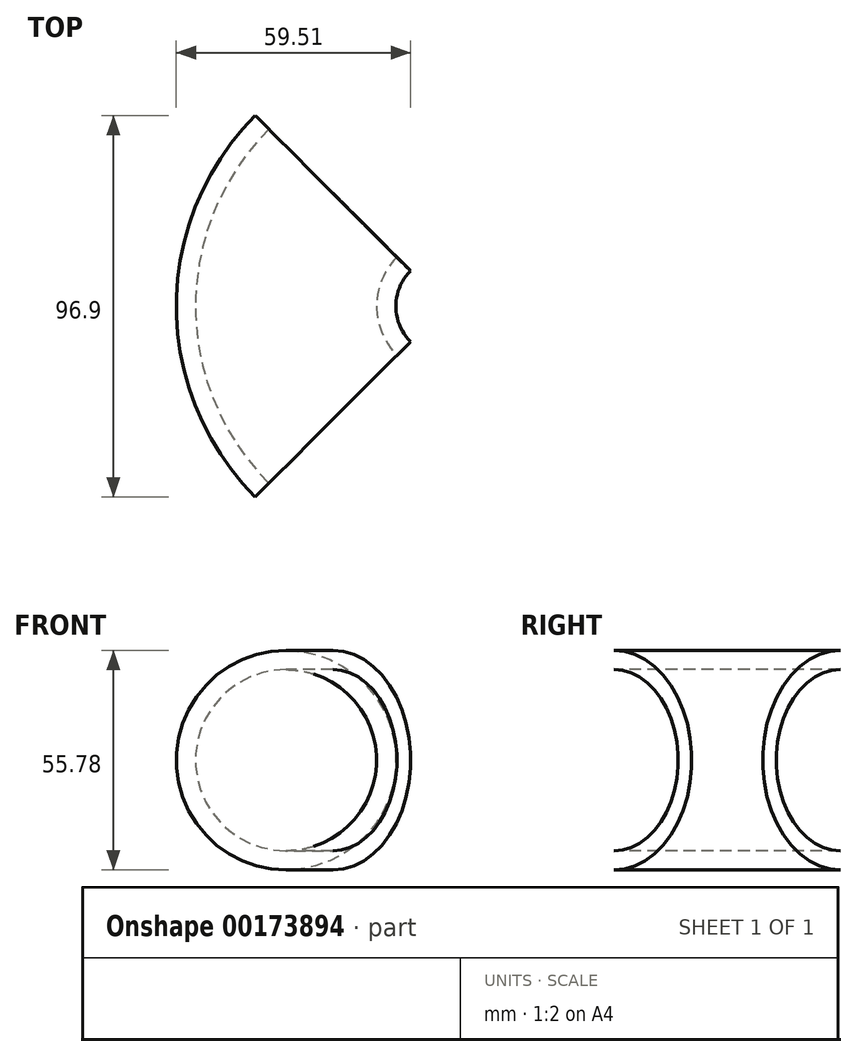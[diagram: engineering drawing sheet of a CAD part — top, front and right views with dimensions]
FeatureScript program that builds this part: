
annotation { "Feature Type Name" : "Feature", "Feature Type Description" : "" }
export const myFeature = defineFeature(function(context is Context, id is Id, definition is map)
    precondition{}
    {
        {
            var Q0;
            Q0=qCreatedBy(makeId("Front.planeOp"),FACE);
            var sketch = newSketch(context, id + "F0", { "sketchPlane" : qUnion([Q0])});
            skCircle(sketch, "E0", {"center": v(0, 0) * mm, "radius": 23 * mm});
            skCircle(sketch, "E1", {"center": v(0, 0) * mm, "radius": 27.9 * mm});
            skLineSegment(sketch, "E2", {"start": v(40.62, 32.36) * mm, "end": v(40.62, -33.94) * mm, "construction": true});
            skLineSegment(sketch, "E3", {"start": v(40.62, -33.94) * mm, "end": v(0, 41.27) * mm, "construction": true});
            skLineSegment(sketch, "E4", {"start": v(0, 41.27) * mm, "end": v(0, -48.35) * mm, "construction": true});
            skSolve(sketch);
        }
        {
            var Q0;
            Q0=makeQuery(id+"F0.imprint","IMPRINT",FACE,{"disambiguationData":[TD([[makeQuery(id+"F0.imprint","IMPRINT",EDGE,{"derivedFrom":sQuery(id+"F0.wireOp",EDGE,"E0")}),-1.0]])]});
            var Q1;
            Q1=sQuery(id+"F0.wireOp",EDGE,"E2");
            revolve(context, id + "F1", {"entities" : qUnion([Q0]), "axis" : qUnion([Q1]), "revolveType" : RevolveType.SYMMETRIC, "angle" : 90 * degree});
        }
    });
